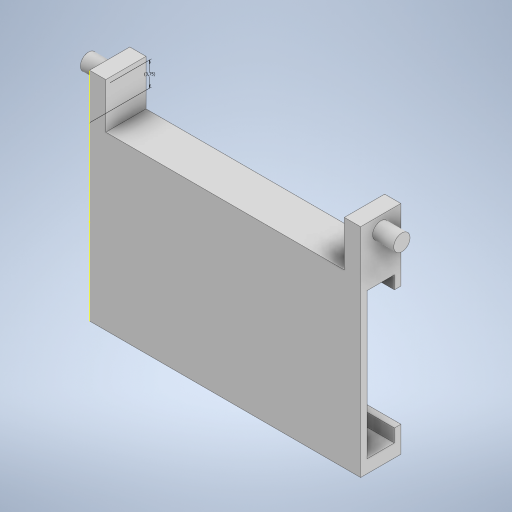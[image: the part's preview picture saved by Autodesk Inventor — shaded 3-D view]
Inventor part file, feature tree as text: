
AUTODESK INVENTOR PART (.ipt)
format: ipt  version: 2024 (Build 280153000, 153)  size: 297,984 bytes
history: native  units: mm
features: sketch x7, extrude x6, mirror x2
ambient origin geometry x8: Origin, YZ Plane, XZ Plane, XY Plane, X Axis, Y Axis, Z Axis, Center Point
bodies: Volumenkörper1 (feature_tree)
feature tree (15):
  extrude  "Extrusion1"  Depth=5.2mm TaperAngle=0.0deg
  extrude  "Extrusion2"  Depth=39.7mm
  extrude  "Extrusion3"  Depth=1.0mm
  extrude  "Extrusion7"  Depth=2.0mm
  mirror  "Spiegeln2"
  extrude  "Extrusion8"  Depth=2.0mm
  extrude  "Extrusion9"  Depth=2.0mm
  mirror  "Spiegeln3"
  sketch  "Skizze10"  dims[d39=2.5mm d40=0.3mm d41=-8.726646mm d42=2.5mm d43=7.0mm d44=0.0mm d45=2.0mm d46=2.5mm d47=3.25mm d48=0.0mm d49=3.75mm]
  sketch  "Skizze1"  dims[d2=1.0mm d3=0.0mm d6=5.2mm d7=0.0mm]
  sketch  "Skizze2"  dims[d11=1.0mm d12=0.0mm d24=39.7mm]
  sketch  "Skizze3"  dims[d25=22.4mm d26=1.0mm]
  sketch  "Skizze7"  dims[d27=0.0mm d30=2.0mm]
  sketch  "Skizze8"  dims[d31=2.0mm d35=2.0mm]
  sketch  "Skizze9"  dims[d36=2.0mm d38=1.5mm]
